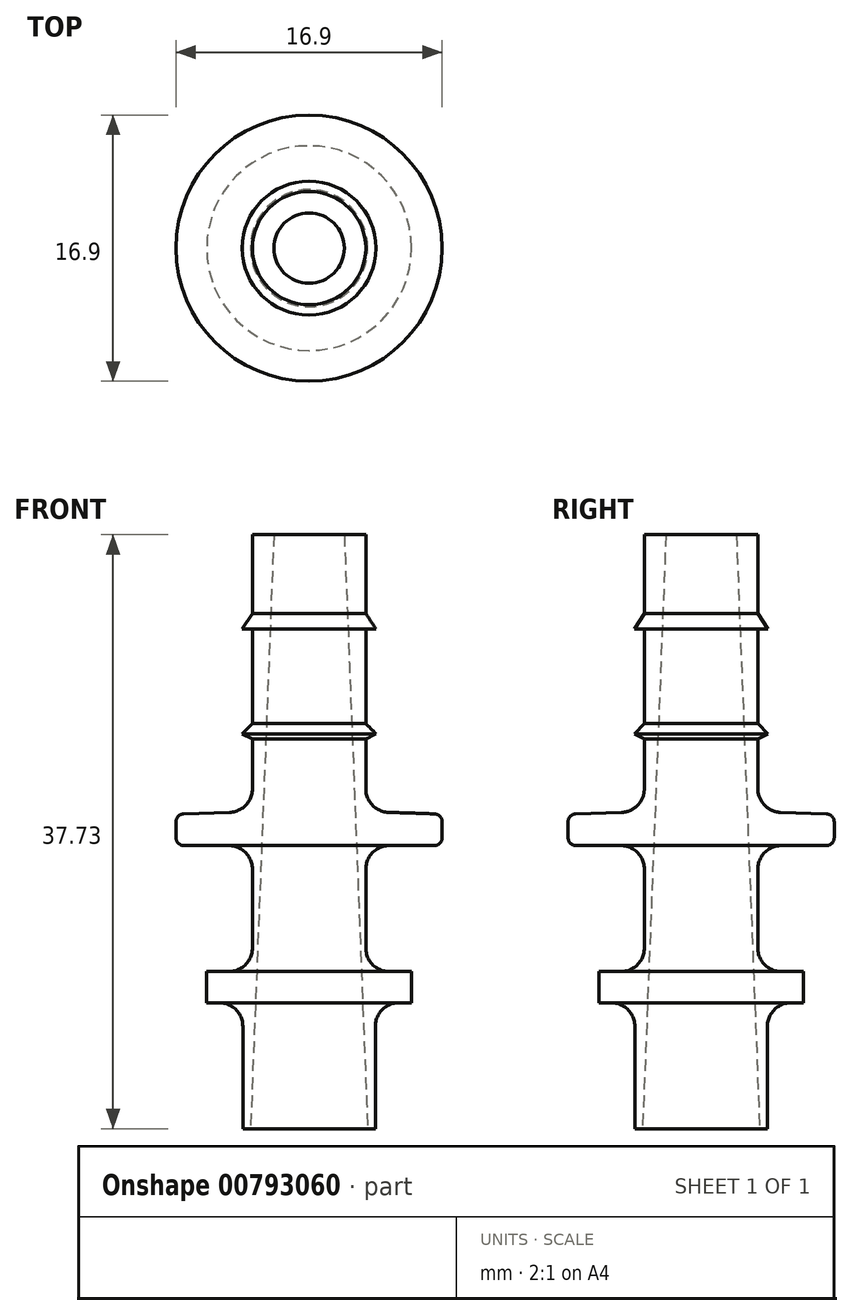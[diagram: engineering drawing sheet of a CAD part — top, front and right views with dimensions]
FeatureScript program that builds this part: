
annotation { "Feature Type Name" : "Feature", "Feature Type Description" : "" }
export const myFeature = defineFeature(function(context is Context, id is Id, definition is map)
    precondition{}
    {
        {
            var Q0;
            Q0=qCreatedBy(makeId("Front.planeOp"),FACE);
            var sketch = newSketch(context, id + "F0", { "sketchPlane" : qUnion([Q0])});
            skLineSegment(sketch, "E0", {"start": v(3.6, 52.85) * mm, "end": v(3.6, 47.85) * mm});
            skLineSegment(sketch, "E1", {"start": v(3.6, 46.85) * mm, "end": v(3.6, 40.85) * mm});
            skLineSegment(sketch, "E2", {"start": v(3.6, 39.86) * mm, "end": v(3.6, 36.71) * mm});
            skLineSegment(sketch, "E3", {"start": v(3.6, 31.6) * mm, "end": v(3.6, 26.6) * mm});
            skLineSegment(sketch, "E4", {"start": v(4.21, 21.62) * mm, "end": v(4.21, 15.12) * mm});
            skLineSegment(sketch, "E5", {"start": v(3.6, 39.86) * mm, "end": v(4.25, 40.2) * mm});
            skLineSegment(sketch, "E6", {"start": v(5.05, 35.21) * mm, "end": v(7.97, 35.12) * mm});
            skLineSegment(sketch, "E7", {"start": v(5.1, 33.1) * mm, "end": v(7.95, 33.1) * mm});
            skLineSegment(sketch, "E8", {"start": v(8.45, 33.6) * mm, "end": v(8.45, 34.62) * mm});
            skPoint(sketch, "E9.endSnap0", {"position": v(6.03, 35.18) * mm});
            skLineSegment(sketch, "E10", {"start": v(0, 52.85) * mm, "end": v(0, 15.25) * mm});
            skPoint(sketch, "E11.visualSharp", {"position": v(3.6, 35.26) * mm});
            skArc(sketch, "E11.filletArc", {"start": v(3.6, 36.71) * mm, "mid": v(4.02, 35.67) * mm, "end": v(5.05, 35.21) * mm});
            skPoint(sketch, "E12.visualSharp", {"position": v(3.6, 33.1) * mm});
            skArc(sketch, "E12.filletArc", {"start": v(5.1, 33.1) * mm, "mid": v(4.04, 32.66) * mm, "end": v(3.6, 31.6) * mm});
            skPoint(sketch, "E13.visualSharp", {"position": v(3.6, 25.1) * mm});
            skArc(sketch, "E13.filletArc", {"start": v(3.6, 26.6) * mm, "mid": v(4.04, 25.54) * mm, "end": v(5.1, 25.1) * mm});
            skPoint(sketch, "E14.visualSharp", {"position": v(4.21, 23.12) * mm});
            skArc(sketch, "E14.filletArc", {"start": v(5.71, 23.12) * mm, "mid": v(4.65, 22.68) * mm, "end": v(4.21, 21.62) * mm});
            skLineSegment(sketch, "E15", {"start": v(3.6, 46.85) * mm, "end": v(4.25, 46.85) * mm});
            skPoint(sketch, "E16.visualSharp", {"position": v(4.74, 46.85) * mm});
            skPoint(sketch, "E17.visualSharp", {"position": v(8.45, 35.1) * mm});
            skArc(sketch, "E17.filletArc", {"start": v(8.45, 34.62) * mm, "mid": v(8.3, 34.96) * mm, "end": v(7.97, 35.12) * mm});
            skPoint(sketch, "E18.visualSharp", {"position": v(8.45, 33.1) * mm});
            skArc(sketch, "E18.filletArc", {"start": v(7.95, 33.1) * mm, "mid": v(8.3, 33.25) * mm, "end": v(8.45, 33.6) * mm});
            skLineSegment(sketch, "E19", {"start": v(3.6, 40.85) * mm, "end": v(4.25, 40.2) * mm});
            skLineSegment(sketch, "E20", {"start": v(5.1, 25.1) * mm, "end": v(6.5, 25.1) * mm});
            skLineSegment(sketch, "E21", {"start": v(5.71, 23.12) * mm, "end": v(6.5, 23.12) * mm});
            skLineSegment(sketch, "E22", {"start": v(6.5, 23.12) * mm, "end": v(6.5, 25.1) * mm});
            skLineSegment(sketch, "E23", {"start": v(3.6, 52.85) * mm, "end": v(2.24, 52.85) * mm});
            skLineSegment(sketch, "E24", {"start": v(2.24, 52.85) * mm, "end": v(3.72, 15.12) * mm});
            skLineSegment(sketch, "E25", {"start": v(3.72, 15.12) * mm, "end": v(4.21, 15.12) * mm});
            skLineSegment(sketch, "E26", {"start": v(3.6, 47.85) * mm, "end": v(4.25, 46.85) * mm});
            skSolve(sketch);
        }
        {
            var Q0;
            Q0=makeQuery(id+"F0.imprint","IMPRINT",FACE,{"disambiguationData":[TD([[makeQuery(id+"F0.imprint","IMPRINT",EDGE,{"derivedFrom":sQuery(id+"F0.wireOp",EDGE,"E0")}),-1.0]])]});
            var Q1;
            Q1=sQuery(id+"F0.wireOp",EDGE,"E10");
            revolve(context, id + "F1", {"surfaceOperationType" : NewSurfaceOperationType.NEW, "entities" : qUnion([Q0]), "axis" : qUnion([Q1]), "revolveType" : RevolveType.FULL});
        }
    });
